# Revit family: Building-ConnessioniIEC309-GEWISS-COMBIBLOC_QUADRETTO_3PRESE
name_source: partatom
category: Apparecchi elettrici
units: mm (PartAtom-declared; Revit-internal decimal feet)

## family parameters
Condiviso = No
Host = Superficie
Mantenere orientamento annotazione = Sì
Punto di calcolo locali = Sì
Quota connettore circolare = Usa diametro
Taglio con vuoti quando caricato = No
Tipo di parte = Normale

## types (1)
- GW66493 - QUADR.IP55 VUOTO VERT. COMBIBLOC 3 PRESE
    Catalogo = BUILDING
    Classe isolamento = II
    Codice Electrocod = 0321
    Colore = Grigio RAL 7035
    Conformità normativa = EN 62208
    Descrizione = QUADR.IP55 VUOTO VERT. COMBIBLOC 3 PRESE
    Dotazioni = 70 °C
    Glow Wire Test = 650°C
    Glow wire test: = Vuoto
    Grado di protezione = IP55
    IDF = 8bd59a7b-e8f2-45cf-adba-4851684e172a
    IDT = 14a8f57f4a104a09a3fed701f6578634
    Modello = GW66493
    N. flange in dotazione = 1
    N. mod. EN 50022 = 12
    N. prese IB alloggiabili: = 3 COMBIBLOC 16/32A
    Per prese: = Compatte
    Potenza dissipabile (W) = 24
    Produttore = GEWISS S.p.A.
    Prospetto di default = 1219 mm
    Resistenza agli urti = IK08
    SEO = Quadretto
    STRUTTURA = RAL - 7035
    STRUTTURA ALTA = Poche
    Scheda Tecnica = https://www.gewiss.com
    Spostamento_S = 1420 mm  [stored 4.65879 ft]
    Temperatura di utilizzo = -25 +40 °C
    Termopressione con biglia = 70 °C
    Tipo versione = Vuoto
    Tipologia di installazione = Da parete
    URL = https://www.gewiss.com
    Versione file RFA = 21.10

note: [stored X ft] marks values corroborated as IEEE doubles in the binary element streams (Revit-internal decimal feet)

## geometry (parser evidence)
native form markers: Sweep x1
no freeform markers — native parametric forms only
